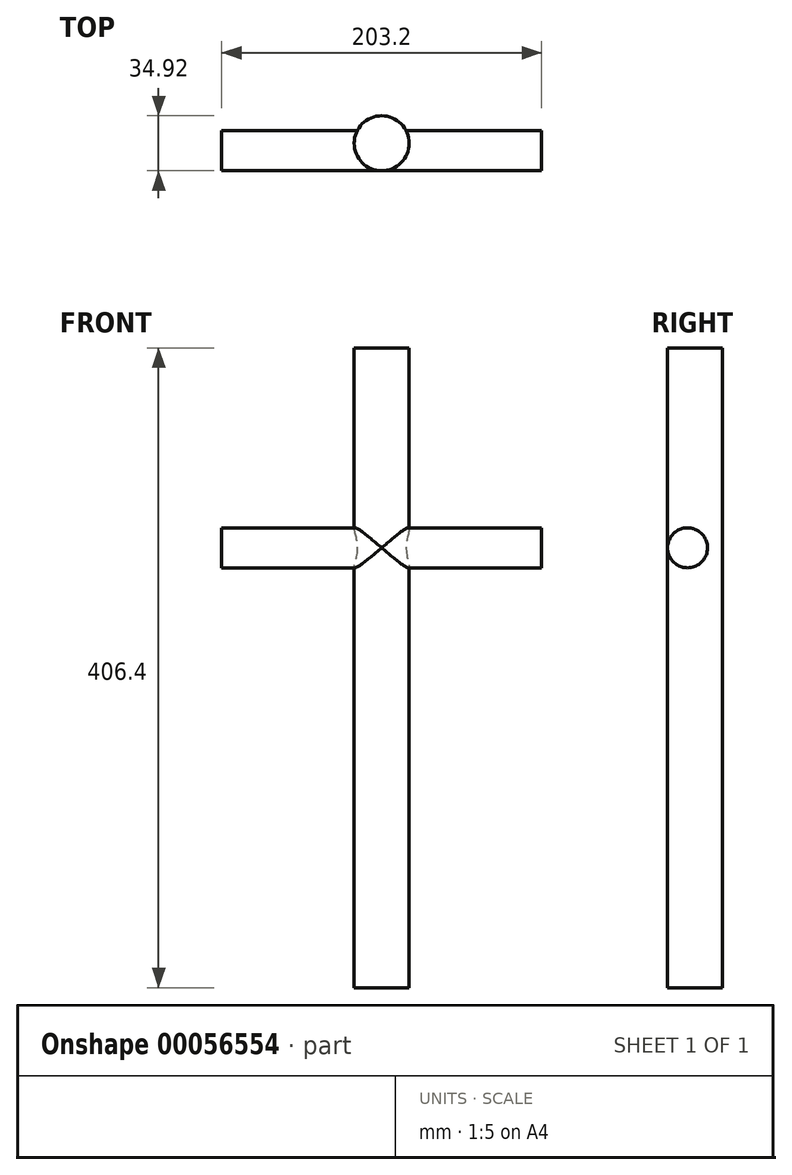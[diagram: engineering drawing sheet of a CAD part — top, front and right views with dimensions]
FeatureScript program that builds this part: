
annotation { "Feature Type Name" : "Feature", "Feature Type Description" : "" }
export const myFeature = defineFeature(function(context is Context, id is Id, definition is map)
    precondition{}
    {
        {
            var Q0;
            Q0=qCreatedBy(makeId("Top.planeOp"),FACE);
            var sketch = newSketch(context, id + "F0", { "sketchPlane" : qUnion([Q0])});
            skCircle(sketch, "E0", {"center": v(0, 0) * mm, "radius": 17.46 * mm});
            skSolve(sketch);
        }
        {
            var Q0;
            Q0=makeQuery(id+"F0.imprint","IMPRINT",FACE,{"disambiguationData":[TD([[makeQuery(id+"F0.imprint","IMPRINT",EDGE,{"derivedFrom":sQuery(id+"F0.wireOp",EDGE,"E0")}),1.0]])]});
            extrude(context, id + "F1", {"entities" : qUnion([Q0]), "oppositeDirection" : true, "depth" : 279.4 * mm});
        }
        {
            var Q0;
            Q0=makeQuery(id+"F1.opExtrude","CAP_FACE",FACE,{"disambiguationData":[OSD([sQuery(id+"F0.wireOp",EDGE,"E0")])],"isStart":true});
            extrude(context, id + "F2", {"entities" : qUnion([Q0]), "operationType" : NewBodyOperationType.ADD, "depth" : 127 * mm});
        }
        {
            var Q0;
            Q0=qCreatedBy(makeId("Right.planeOp"),FACE);
            var sketch = newSketch(context, id + "F3", { "sketchPlane" : qUnion([Q0])});
            skCircle(sketch, "E1", {"center": v(-4.76, 0) * mm, "radius": 12.7 * mm});
            skSolve(sketch);
        }
        {
            var Q0;
            Q0=qSketchRegion(id+"F3",true);
            extrude(context, id + "F4", {"entities" : qUnion([Q0]), "operationType" : NewBodyOperationType.ADD, "depth" : 101.6 * mm});
        }
        {
            var Q0;
            Q0=qSketchRegion(id+"F3",true);
            extrude(context, id + "F5", {"entities" : qUnion([Q0]), "operationType" : NewBodyOperationType.ADD, "oppositeDirection" : true, "depth" : 101.6 * mm});
        }
    });
